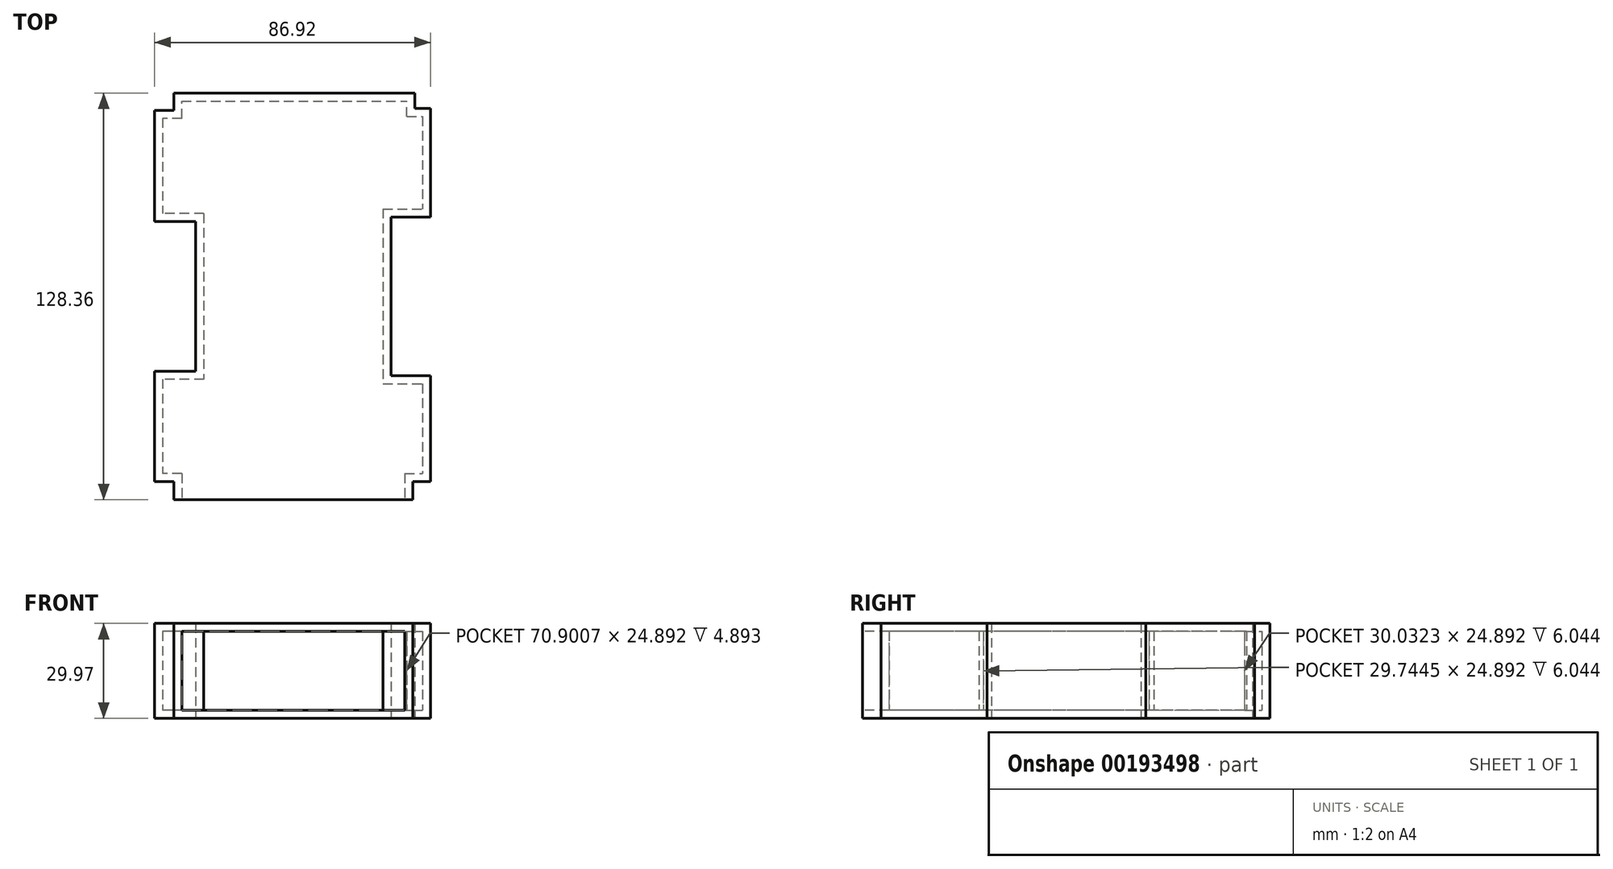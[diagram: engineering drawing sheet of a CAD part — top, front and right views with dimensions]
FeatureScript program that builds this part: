
annotation { "Feature Type Name" : "Feature", "Feature Type Description" : "" }
export const myFeature = defineFeature(function(context is Context, id is Id, definition is map)
    precondition{}
    {
        {
            var Q0;
            Q0=qCreatedBy(makeId("Top.planeOp"),FACE);
            var sketch = newSketch(context, id + "F0", { "sketchPlane" : qUnion([Q0])});
            skLineSegment(sketch, "E0.bottom", {"start": v(-37.41, 64.18) * mm, "end": v(38.57, 64.18) * mm});
            skLineSegment(sketch, "E0.top", {"start": v(-37.41, -64.18) * mm, "end": v(38, -64.18) * mm});
            skLineSegment(sketch, "E0.left", {"start": v(-43.46, 58.71) * mm, "end": v(-43.46, 23.6) * mm});
            skLineSegment(sketch, "E0.right", {"start": v(43.46, 59.29) * mm, "end": v(43.46, 25.04) * mm});
            skPoint(sketch, "E0.middle", {"position": v(0, 0) * mm});
            skLineSegment(sketch, "E1.bottom", {"start": v(-30.5, 23.6) * mm, "end": v(-43.46, 23.6) * mm});
            skLineSegment(sketch, "E1.top", {"start": v(-30.5, -23.6) * mm, "end": v(-43.46, -23.6) * mm});
            skLineSegment(sketch, "E1.left", {"start": v(-30.5, 23.6) * mm, "end": v(-30.5, -23.6) * mm});
            skPoint(sketch, "E1.middle", {"position": v(-43.46, 0) * mm});
            skPoint(sketch, "E1.right.start.orphan", {"position": v(-56.4, 23.6) * mm});
            skPoint(sketch, "E2.orphan", {"position": v(-56.4, -23.6) * mm});
            skLineSegment(sketch, "E3.trimOffspring", {"start": v(-43.46, -23.6) * mm, "end": v(-43.46, -58.42) * mm});
            skLineSegment(sketch, "E4.bottom", {"start": v(31.08, 25.04) * mm, "end": v(43.46, 25.04) * mm});
            skLineSegment(sketch, "E4.top", {"start": v(31.08, -25.04) * mm, "end": v(43.46, -25.04) * mm});
            skLineSegment(sketch, "E4.left", {"start": v(31.08, 25.04) * mm, "end": v(31.08, -25.04) * mm});
            skPoint(sketch, "E4.middle", {"position": v(43.46, 0) * mm});
            skPoint(sketch, "E4.right.start.orphan", {"position": v(55.83, 25.04) * mm});
            skLineSegment(sketch, "E5.trimOffspring", {"start": v(43.46, -25.04) * mm, "end": v(43.46, -58.42) * mm});
            skPoint(sketch, "E6.orphan", {"position": v(55.83, -25.04) * mm});
            skLineSegment(sketch, "E7.bottom", {"start": v(-37.41, 58.71) * mm, "end": v(-43.46, 58.71) * mm});
            skLineSegment(sketch, "E7.left", {"start": v(-37.41, 58.71) * mm, "end": v(-37.41, 64.18) * mm});
            skPoint(sketch, "E7.middle", {"position": v(-43.46, 64.18) * mm});
            skPoint(sketch, "E7.right.start.orphan", {"position": v(-49.5, 58.71) * mm});
            skPoint(sketch, "E7.top.end.orphan", {"position": v(-49.5, 69.65) * mm});
            skPoint(sketch, "E8.orphan", {"position": v(-37.41, 69.65) * mm});
            skLineSegment(sketch, "E9.bottom", {"start": v(38.57, 59.29) * mm, "end": v(43.46, 59.29) * mm});
            skLineSegment(sketch, "E9.left", {"start": v(38.57, 59.29) * mm, "end": v(38.57, 64.18) * mm});
            skPoint(sketch, "E9.middle", {"position": v(43.46, 64.18) * mm});
            skPoint(sketch, "E9.right.start.orphan", {"position": v(48.35, 59.29) * mm});
            skPoint(sketch, "E9.top.end.orphan", {"position": v(48.35, 69.07) * mm});
            skPoint(sketch, "E9.top.start.orphan", {"position": v(38.57, 69.07) * mm});
            skLineSegment(sketch, "E10.bottom", {"start": v(-37.41, -58.42) * mm, "end": v(-43.46, -58.42) * mm});
            skLineSegment(sketch, "E10.left", {"start": v(-37.41, -58.42) * mm, "end": v(-37.41, -64.18) * mm});
            skPoint(sketch, "E10.middle", {"position": v(-43.46, -64.18) * mm});
            skLineSegment(sketch, "E11.bottom", {"start": v(38, -58.42) * mm, "end": v(43.46, -58.42) * mm});
            skLineSegment(sketch, "E11.left", {"start": v(38, -58.42) * mm, "end": v(38, -64.18) * mm});
            skPoint(sketch, "E11.middle", {"position": v(43.46, -64.18) * mm});
            skPoint(sketch, "E10.right.start.orphan", {"position": v(-49.5, -58.42) * mm});
            skPoint(sketch, "E10.top.end.orphan", {"position": v(-49.5, -69.94) * mm});
            skPoint(sketch, "E10.top.start.orphan", {"position": v(-37.41, -69.94) * mm});
            skPoint(sketch, "E11.top.start.orphan", {"position": v(38, -69.94) * mm});
            skPoint(sketch, "E11.right.end.orphan", {"position": v(48.93, -69.94) * mm});
            skPoint(sketch, "E11.right.start.orphan", {"position": v(48.93, -58.42) * mm});
            skSolve(sketch);
        }
        {
            var Q0;
            Q0=makeQuery(id+"F0.imprint","IMPRINT",FACE,{"disambiguationData":[TD([[makeQuery(id+"F0.imprint","IMPRINT",EDGE,{"derivedFrom":sQuery(id+"F0.wireOp",EDGE,"E0.bottom")}),-1.0]])]});
            extrude(context, id + "F1", {"entities" : qUnion([Q0]), "depth" : 29.97 * mm});
        }
        {
            var Q0;
            Q0=makeQuery(id+"F1.opExtrude","SWEPT_FACE",FACE,{"disambiguationData":[OSD([sQuery(id+"F0.wireOp",EDGE,"E0.top")])]});
            shell(context, id + "F2", {"entities" : qUnion([Q0]), "thickness" : 2.54 * mm});
        }
    });
